# Revit family: Shelves
name_source: partatom
category: Furniture
units: mm (PartAtom-declared; Revit-internal decimal feet)

## family parameters
Always vertical = Yes
Cut with Voids When Loaded = No
OmniClass Number = 23.40.20.00
OmniClass Title = General Furniture and Specialties
Room Calculation Point = No
Shared = No
Work Plane-Based = No

## types (9) — shared parameters
AssetType = Fixed
Category = PR_40_30_78_57
Color = Vision Pallete
DurationUnit = Years
ExpectedLife = 10
Finish = Powder Coated Steel
Height = 18 mm  [stored 0.0590551 ft]
Keynote = PR_40_30_78_57
ManufacturerName = Bisley
ManufacturerURL = www.bisley.com
NBSDescription = Office storage
NBSReference = 45-35-80/360
NominalHeight = 18 mm  [stored 0.0590551 ft]
Shape = Rectangular
URL = www.bisley.com
Uniclass2015Code = PR_40_30_78_57
Uniclass2015Title = 78 - Shelves and Storage Units
Uniclass2015Version = V1.1
WarrantyDescription = Standard Bisley Warranty
WarrantyDurationUnit = Year
zero-valued in all types: Default Elevation

## per-type parameters (varying)
| type | Depth | Material | NominalLength | NominalWidth | Width |
| Steel Shelf 1000w units | 358 mm  [stored 1.17454 ft] | Steel | 358 mm  [stored 1.17454 ft] | 468 mm  [stored 1.53543 ft] | 468 mm  [stored 1.53543 ft] |
| Steel Shelf 800w units | 358 mm  [stored 1.17454 ft] | Steel | 358 mm  [stored 1.17454 ft] | 368 mm  [stored 1.20735 ft] | 368 mm  [stored 1.20735 ft] |
| MFC Shelf 800w units | 358 mm  [stored 1.17454 ft] | MFC | 358 mm  [stored 1.17454 ft] | 368 mm  [stored 1.20735 ft] | 368 mm  [stored 1.20735 ft] |
| MFC Shelf 1000w units | 358 mm  [stored 1.17454 ft] | MFC | 358 mm  [stored 1.17454 ft] | 468 mm  [stored 1.53543 ft] | 468 mm  [stored 1.53543 ft] |
| Steel Shelf 1000w units 470 deep | 428 mm  [stored 1.4042 ft] | Steel | 428 mm  [stored 1.4042 ft] | 468 mm  [stored 1.53543 ft] | 468 mm  [stored 1.53543 ft] |
| MFC Shelf 1000w units 470d | 428 mm  [stored 1.4042 ft] | MFC | 428 mm  [stored 1.4042 ft] | 468 mm  [stored 1.53543 ft] | 468 mm  [stored 1.53543 ft] |
| MFC Shelf 800w units 470d | 428 mm  [stored 1.4042 ft] | MFC | 428 mm  [stored 1.4042 ft] | 368 mm  [stored 1.20735 ft] | 368 mm  [stored 1.20735 ft] |
| Steel Shelf 800w units 470d | 428 mm  [stored 1.4042 ft] | Steel | 428 mm  [stored 1.4042 ft] | 368 mm  [stored 1.20735 ft] | 368 mm  [stored 1.20735 ft] |
| Steel Shelf 400w x 400w | 358 mm  [stored 1.17454 ft] | Steel | 358 mm  [stored 1.17454 ft] | 358 mm  [stored 1.17454 ft] | 358 mm  [stored 1.17454 ft] |

note: [stored X ft] marks values corroborated as IEEE doubles in the binary element streams (Revit-internal decimal feet)

## geometry (parser evidence)
native form markers: Sweep x3
no freeform markers — native parametric forms only
